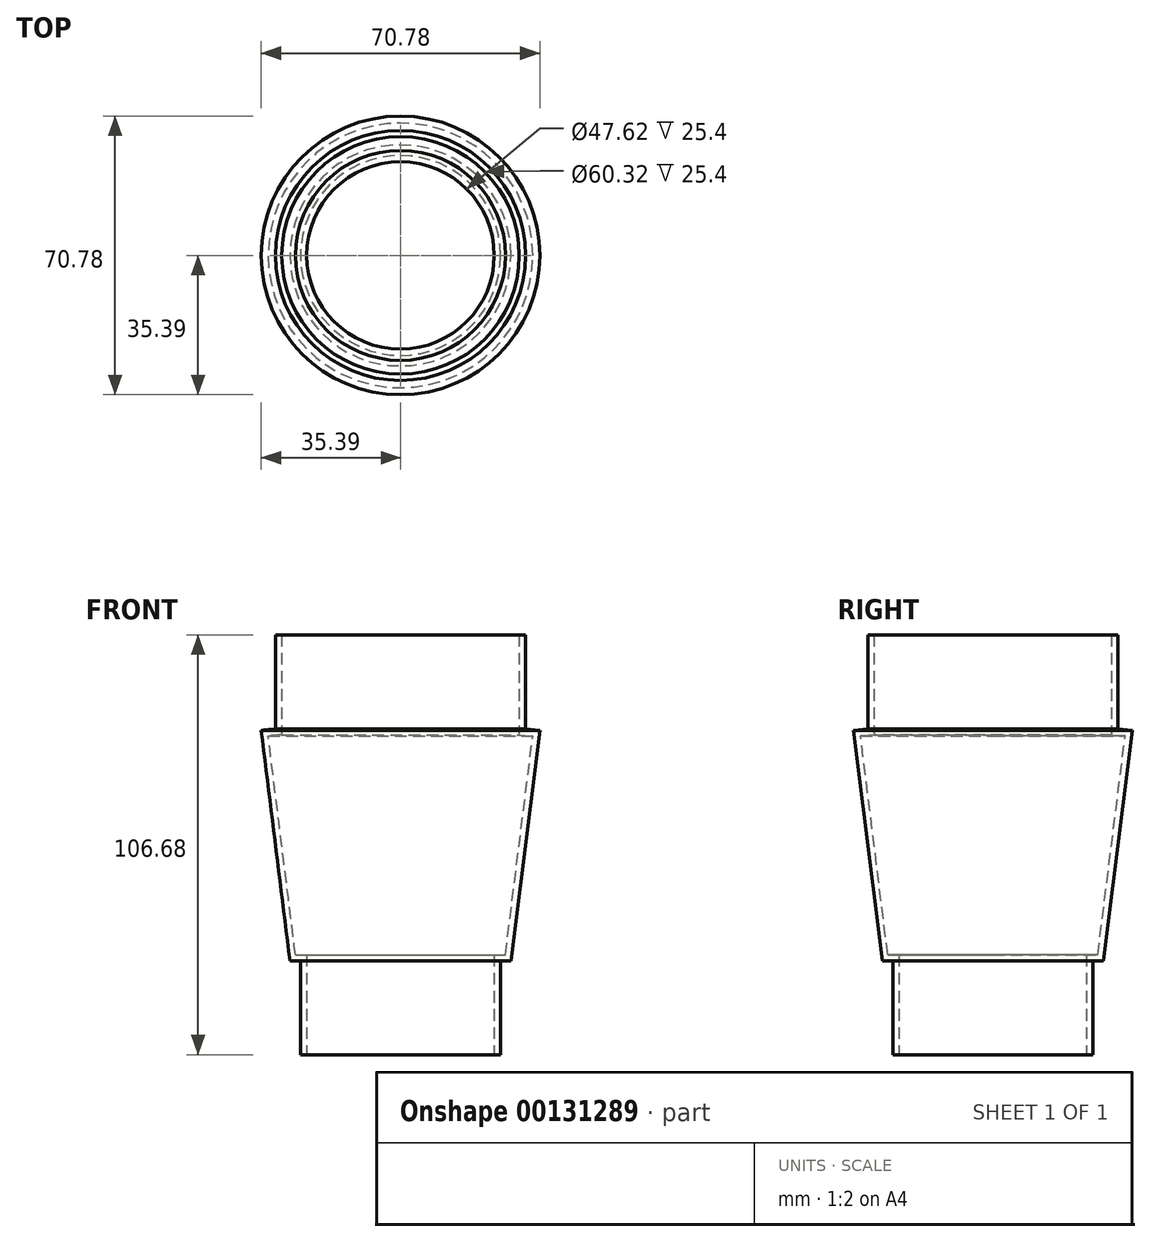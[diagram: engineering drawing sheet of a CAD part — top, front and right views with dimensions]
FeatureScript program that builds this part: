
annotation { "Feature Type Name" : "Feature", "Feature Type Description" : "" }
export const myFeature = defineFeature(function(context is Context, id is Id, definition is map)
    precondition{}
    {
        {
            var Q0;
            Q0=qCreatedBy(makeId("Front.planeOp"),FACE);
            var sketch = newSketch(context, id + "F0", { "sketchPlane" : qUnion([Q0])});
            skLineSegment(sketch, "E0", {"start": v(33.62, 0) * mm, "end": v(30.16, 0.32) * mm});
            skLineSegment(sketch, "E1", {"start": v(23.81, -55.56) * mm, "end": v(26.67, -55.56) * mm});
            skLineSegment(sketch, "E2", {"start": v(26.67, -55.56) * mm, "end": v(33.62, 0) * mm});
            skLineSegment(sketch, "E3", {"start": v(30.16, 25.72) * mm, "end": v(30.16, 0.32) * mm});
            skLineSegment(sketch, "E4", {"start": v(23.81, -80.96) * mm, "end": v(23.81, -55.56) * mm});
            skLineSegment(sketch, "E5.0", {"start": v(31.75, 25.72) * mm, "end": v(31.75, 1.77) * mm});
            skLineSegment(sketch, "E5.1", {"start": v(25.4, -80.96) * mm, "end": v(25.4, -57.15) * mm});
            skLineSegment(sketch, "E5.2", {"start": v(25.4, -57.15) * mm, "end": v(28.07, -57.15) * mm});
            skLineSegment(sketch, "E5.3", {"start": v(28.07, -57.15) * mm, "end": v(35.4, 1.43) * mm});
            skLineSegment(sketch, "E5.4", {"start": v(35.4, 1.43) * mm, "end": v(31.75, 1.77) * mm});
            skLineSegment(sketch, "E6", {"start": v(23.81, -80.96) * mm, "end": v(25.4, -80.96) * mm});
            skLineSegment(sketch, "E7", {"start": v(31.75, 25.72) * mm, "end": v(30.16, 25.72) * mm});
            skLineSegment(sketch, "E8", {"start": v(0, -68.26) * mm, "end": v(0, 12.7) * mm});
            skLineSegment(sketch, "E9", {"start": v(0, -68.26) * mm, "end": v(0, -80.96) * mm});
            skLineSegment(sketch, "E10", {"start": v(0, 12.7) * mm, "end": v(0, 25.72) * mm});
            skSolve(sketch);
        }
        {
            var Q0;
            Q0=makeQuery(id+"F0.imprint","IMPRINT",FACE,{"disambiguationData":[TD([[makeQuery(id+"F0.imprint","IMPRINT",EDGE,{"derivedFrom":sQuery(id+"F0.wireOp",EDGE,"E0")}),-1.0]])]});
            var Q1;
            Q1=sQuery(id+"F0.wireOp",EDGE,"E8");
            revolve(context, id + "F1", {"entities" : qUnion([Q0]), "axis" : qUnion([Q1]), "revolveType" : RevolveType.FULL});
        }
    });
